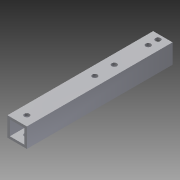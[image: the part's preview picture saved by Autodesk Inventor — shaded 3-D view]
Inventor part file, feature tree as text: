
AUTODESK INVENTOR PART (.ipt)
format: ipt  version: 2013 (Build 170138000, 138)  size: 111,616 bytes
history: native  units: in
note: dims shown in document units (in); Inventor stores cm internally (conversion verified against a paired STEP export)
features: extrude x4, sketch x4, reference x4
ambient origin geometry x8: Origin, YZ Plane, XZ Plane, XY Plane, X Axis, Y Axis, Z Axis, Center Point
bodies: Solid1 (feature_tree)
feature tree (12):
  extrude  "Extrusion1"  Depth=1.0in
  extrude  "Extrusion2"  Depth=7.5in TaperAngle=0.0deg
  extrude  "Extrusion3"  Depth=1.0in TaperAngle=0.0deg
  extrude  "Extrusion4"  [1 undecoded]
  sketch  "Sketch1"  dims[d0=1.0in d2=1.0in]
  sketch  "Sketch2"  dims[d3=0.125in d4=7.5in d5=0.0in]
  reference  "Reference1"
  reference  "Reference2"
  sketch  "Sketch3"  dims[d6=1.0in d7=0.0in d8=1.0in d9=0.0in]
  reference  "Reference3"
  reference  "Reference4"
  sketch  "Sketch4"  dims[d10=1.0in d11=0.0in]
note: 1 required parameter value undecoded (feature->parameter linkage not recoverable at this tier; creation-order binding heuristic only, values carry confidence <= 0.55)
